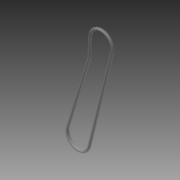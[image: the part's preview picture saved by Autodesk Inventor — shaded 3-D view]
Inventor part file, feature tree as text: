
AUTODESK INVENTOR PART (.ipt)
format: ipt  version: 2014 SP1 (Build 180222100, 222)  size: 119,296 bytes
history: native  units: in
note: dims shown in document units (in); Inventor stores cm internally (conversion verified against a paired STEP export)
features: reference x3, sketch x2, plane x1, sweep x1, other x1
ambient origin geometry x8: Origin, YZ Plane, XZ Plane, XY Plane, X Axis, Y Axis, Z Axis, Center Point
bodies: Solid1 (feature_tree)
feature tree (8):
  sketch  "Sketch1"  dims[d0=0.45in d1=0.7in]
  plane  "Work Plane1"
  sweep  "Sweep1"
  reference  "Reference1"
  reference  "Reference2"
  reference  "Reference3"
  other  "Work Axis1"
  sketch  "Sketch2"  dims[d2=1.66in d3=1.91in d4=1.66in d5=1.91in d6=0.25in d7=0.125in d8=0.0in]
